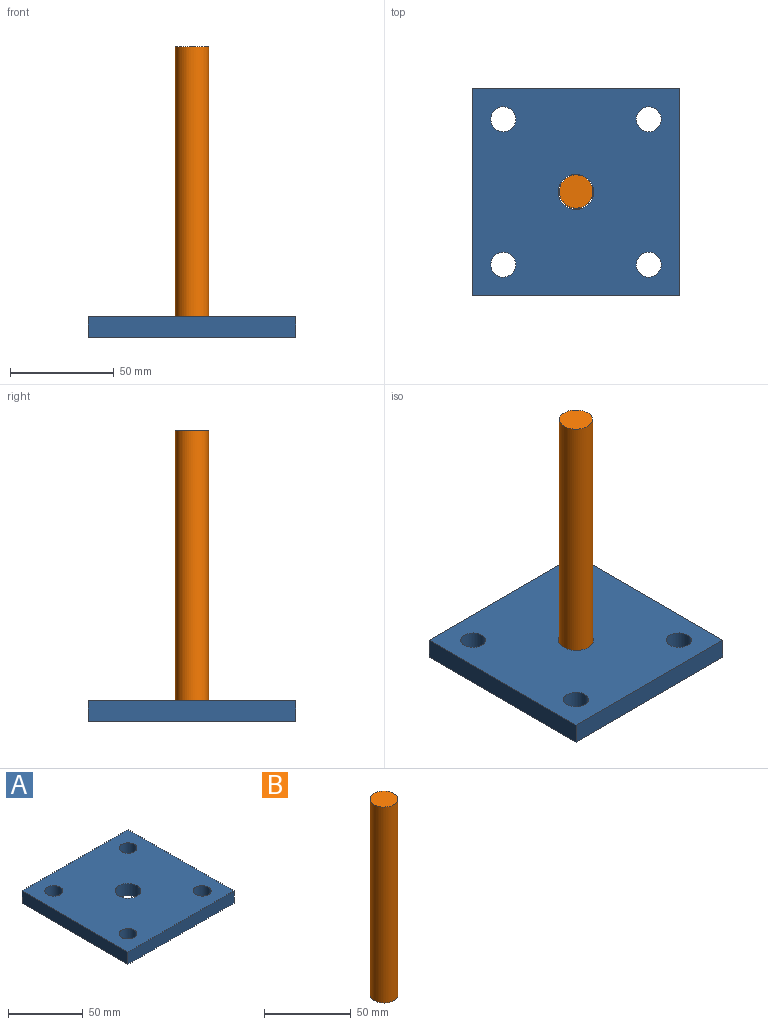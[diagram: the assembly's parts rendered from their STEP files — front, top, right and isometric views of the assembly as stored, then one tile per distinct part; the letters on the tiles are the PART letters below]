
ASSEMBLY  parts=2 mates=1
PART A: 11 faces, bbox 100x100x10 mm
  f0: plane 100x10mm, normal (-1,0,0), area 1000mm2, adj f1,f7,f9,f10
  f1: plane 100x10mm, normal (0,-1,0), area 1000mm2, adj f0,f2,f9,f10
  f2: plane 100x10mm, normal (1,0,0), area 1000mm2, adj f1,f7,f9,f10
  f3: cylinder r=6mm len=12mm, axis (0,0,-1), area 377mm2, adj f9,f10
  f4: cylinder r=6mm len=12mm, axis (0,0,-1), area 377mm2, adj f9,f10
  f5: cylinder r=6mm len=12mm, axis (0,0,-1), area 377mm2, adj f9,f10
  f6: cylinder r=6mm len=12mm, axis (0,0,-1), area 377mm2, adj f9,f10
  f7: plane 100x10mm, normal (0,1,0), area 1000mm2, adj f0,f2,f9,f10
  f8: cylinder r=8.5mm len=17mm, axis (0,0,-1), area 534.1mm2, adj f9,f10
  f9: plane 100x100mm, normal (0,0,1), area 9320.6mm2, adj f0,f1,f2,f3,f4,f5,f6,f7
  f10: plane 100x100mm, normal (0,0,-1), area 9320.6mm2, adj f0,f1,f2,f3,f4,f5,f6,f7
PART B: 3 faces, bbox 16x16x138 mm
  f0: cylinder r=8mm len=138mm, axis (0,0,-1), area 6936.6mm2, adj f1,f2
  f1: plane 16x16mm, normal (0,0,1), area 201.1mm2, adj f0
  f2: plane 16x16mm, normal (0,0,-1), area 201.1mm2, adj f0
PLACE A t=(8.04,4.24,-5.02)mm
PLACE B t=(8.04,4.24,-5.02)mm
MATE cylindrical A.f8 <-> B.f0  axis (0,0,-1) through (8.04,4.24,-5.02)mm
